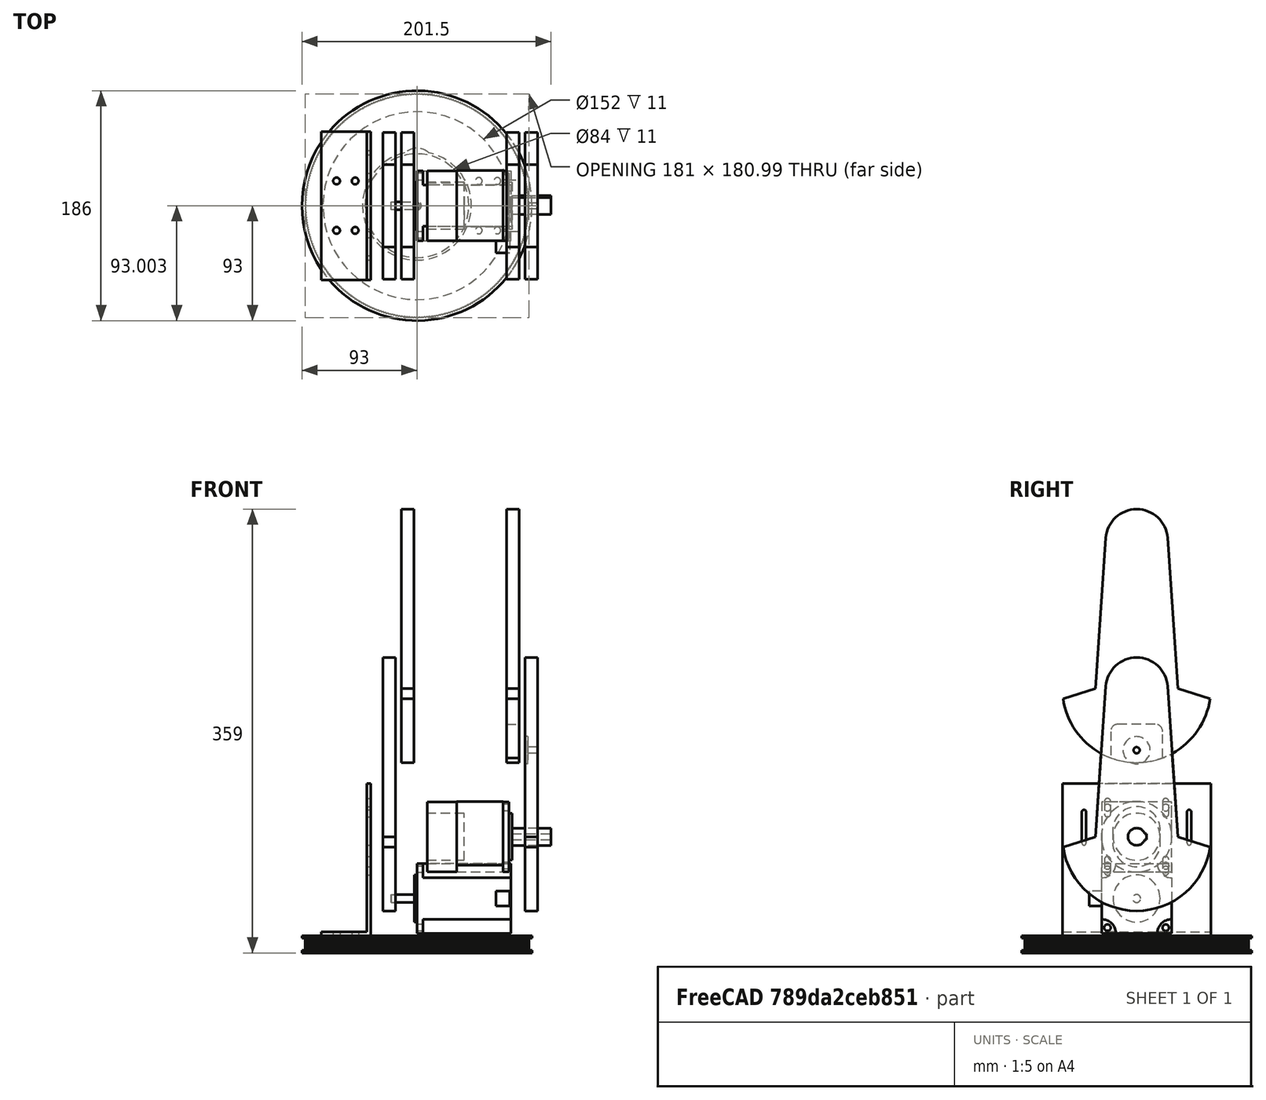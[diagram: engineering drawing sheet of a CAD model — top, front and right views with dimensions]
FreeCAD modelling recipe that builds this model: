
FCSTD DOCUMENT  (FreeCAD 0.21R33771 (Git))
Label: jrobot-y-axis-assembly
License: All rights reserved
LicenseURL: http://en.wikipedia.org/wiki/All_rights_reserved
objects: Part::Feature×26, App::Link×13, Part::MultiCommon×8, App::DocumentObjectGroup×5, App::Part×2, PartDesign::CoordinateSystem×1, App::FeaturePython×1, Part::FeaturePython×1
note: 36 computed .brp shape members not serialized (recipe doc carries the construction recipe); baked Part::Feature solids carry a one-line shape summary decoded from their .brp
EXTERNAL_REF file=jrobot-x-axis-parts.FCStd obj=LCS_X_Axis_Rotor_Origin
EXTERNAL_REF file=jrobot-x-axis-parts.FCStd obj=Part022
EXTERNAL_REF file=jrobot-x-axis-parts.FCStd obj=LCS_1
EXTERNAL_REF file=jrobot-y-axis-parts.FCStd obj=LCS_Y_Axis_Base_Left_Origin
EXTERNAL_REF file=jrobot-y-axis-parts.FCStd obj=Part
EXTERNAL_REF file=jrobot-x-axis-parts.FCStd obj=LCS_Y_Axis_Base_Right
EXTERNAL_REF file=jrobot-y-axis-parts.FCStd obj=LCS_Y_Axis_Arm_Left_Pivot
EXTERNAL_REF file=jrobot-y-axis-parts.FCStd obj=LCS_Y_Axis_Base_Pivot
EXTERNAL_REF file=jrobot-y-axis-parts.FCStd obj=Part001
EXTERNAL_REF file=jrobot-x-axis-parts.FCStd obj=LCS_X_Axis_Rotor_Top
EXTERNAL_REF file=standard-parts.FCStd obj=LCS_Nema23_76mm_MountFace
EXTERNAL_REF file=standard-parts.FCStd obj=Part015
EXTERNAL_REF file=standard-parts.FCStd obj=LCS_Nema23_Gearbox_FLF57_Origin
EXTERNAL_REF file=standard-parts.FCStd obj=Part068
EXTERNAL_REF file=jrobot-y-axis-parts.FCStd obj=LCS_Y_Axis_ZMotor
EXTERNAL_REF file=standard-parts.FCStd obj=LCS_Nema17_42mm_MountFace
EXTERNAL_REF file=standard-parts.FCStd obj=Part001
EXTERNAL_REF file=jrobot-y-axis-parts.FCStd obj=LCS_Y_Axis_ZPivot
EXTERNAL_REF file=jrobot-y-axis-parts.FCStd obj=LCS_Origin
EXTERNAL_REF file=jrobot-y-axis-parts.FCStd obj=Part002
EXTERNAL_REF file=standard-parts.FCStd obj=LCS_Bearing_Printed_Inner_Origin
EXTERNAL_REF file=standard-parts.FCStd obj=Part069
EXTERNAL_REF file=../../../snap/freecad/common/temp/FreeCAD_Doc_96e0f8cd-3bd0-4b8c-b372-3804dd1025b3_da39a3_2601561 obj=LCS_Bearing_Printed_Inner_Origin
EXTERNAL_REF file=../../../snap/freecad/common/temp/FreeCAD_Doc_96e0f8cd-3bd0-4b8c-b372-3804dd1025b3_da39a3_2601561 obj=Part069

FEATURE [App::DocumentObjectGroup] Parts
FEATURE [PartDesign::CoordinateSystem] LCS_Origin
  AttacherType = Attacher::AttachEngine3D
  MapMode = 2
  Support = -> [X_Axis]
FEATURE [App::DocumentObjectGroup] Constraints
FEATURE [App::FeaturePython] Variables  # WARN: FeaturePython — macro-defined, semantics opaque (R4)
  Type = App::PropertyContainer
FEATURE [App::DocumentObjectGroup] Configurations
FEATURE [App::Link] P_X_Axis_Rotor
  AttachedBy = #LCS_X_Axis_Rotor_Origin
  AttachedTo = Parent Assembly#LCS_Origin
  LinkedObject = -> <external jrobot-x-axis-parts.FCStd>#Part022
  SolverId = Asm4EE
  expr: Placement = LCS_Origin.Placement * AttachmentOffset * jrobot_x_axis_parts#LCS_X_Axis_Rotor_Origin.Placement ^ -1
FEATURE [App::Link] P_Y_Axis_Base_Left
  AttachedBy = #LCS_Y_Axis_Base_Left_Origin
  AttachedTo = P_X_Axis_Rotor#LCS_1
  LinkPlacement = pos=(57.5,0,14) rot=(0,0,1;0rad)
  LinkedObject = -> <external jrobot-y-axis-parts.FCStd>#Part
  Placement = pos=(57.5,0,14) rot=(0,0,1;0rad)
  SolverId = Asm4EE
  expr: Placement = P_X_Axis_Rotor.Placement * jrobot_x_axis_parts#LCS_1.Placement * AttachmentOffset * jrobot_y_axis_parts#LCS_Y_Axis_Base_Left_Origin.Placement ^ -1
FEATURE [App::Link] P_Y_Axis_Base_Left_2
  AttachedBy = #LCS_Y_Axis_Base_Left_Origin
  AttachedTo = P_X_Axis_Rotor#LCS_Y_Axis_Base_Right
  LinkPlacement = pos=(-57.5,0,14) rot=(0,0,1;0rad)
  LinkedObject = -> <external jrobot-y-axis-parts.FCStd>#Part
  Placement = pos=(-57.5,0,14) rot=(0,0,1;0rad)
  SolverId = Asm4EE
  expr: Placement = P_X_Axis_Rotor.Placement * jrobot_x_axis_parts#LCS_Y_Axis_Base_Right.Placement * AttachmentOffset * jrobot_y_axis_parts#LCS_Y_Axis_Base_Left_Origin.Placement ^ -1
FEATURE [App::Link] P_Y_Axis_Arm_Left
  AttachedBy = #LCS_Y_Axis_Arm_Left_Pivot
  AttachedTo = P_Y_Axis_Base_Left#LCS_Y_Axis_Base_Pivot
  AttachmentOffset = pos=(-20,0,0) rot=(1,0,0;0rad)
  LinkPlacement = pos=(57.5,0,154) rot=(0,0,1;0rad)
  LinkedObject = -> <external jrobot-y-axis-parts.FCStd>#Part001
  Placement = pos=(57.5,0,154) rot=(0,0,1;0rad)
  SolverId = Asm4EE
  expr: Placement = P_Y_Axis_Base_Left.Placement * jrobot_y_axis_parts#LCS_Y_Axis_Base_Pivot.Placement * AttachmentOffset * jrobot_y_axis_parts#LCS_Y_Axis_Arm_Left_Pivot.Placement ^ -1
FEATURE [App::Link] P_Nema23_76mm
  AttachedBy = #LCS_Nema23_76mm_MountFace
  AttachedTo = P_X_Axis_Rotor#LCS_X_Axis_Rotor_Top
  AttachmentOffset = pos=(30,0,30) rot=(0.57735,-0.57735,-0.57735;2.0944rad)
  LinkPlacement = pos=(106,8.4e-15,44) rot=(0.57735,-0.57735,-0.57735;2.0944rad)
  LinkedObject = -> <external standard-parts.FCStd>#Part015
  Placement = pos=(106,8.4e-15,44) rot=(0.57735,-0.57735,-0.57735;2.0944rad)
  SolverId = Asm4EE
  expr: Placement = P_X_Axis_Rotor.Placement * jrobot_x_axis_parts#LCS_X_Axis_Rotor_Top.Placement * AttachmentOffset * standard_parts#LCS_Nema23_76mm_MountFace.Placement ^ -1
FEATURE [App::Link] P_Nema23_Gearbox_FLF57
  AttachedBy = #LCS_Nema23_Gearbox_FLF57_Origin
  AttachedTo = P_Nema23_76mm#LCS_Nema23_76mm_MountFace
  AttachmentOffset = pos=(0,0,0) rot=(0,0,-1;1.5708rad)
  LinkPlacement = pos=(30,0,44) rot=(0.707107,0,-0.707107;3.14159rad)
  LinkedObject = -> <external standard-parts.FCStd>#Part068
  Placement = pos=(30,0,44) rot=(0.707107,0,-0.707107;3.14159rad)
  SolverId = Asm4EE
  expr: Placement = P_Nema23_76mm.Placement * standard_parts#LCS_Nema23_76mm_MountFace.Placement * AttachmentOffset * standard_parts#LCS_Nema23_Gearbox_FLF57_Origin.Placement ^ -1
FEATURE [App::Link] P_Nema17_33mm
  AttachedBy = #LCS_Nema17_42mm_MountFace
  AttachedTo = P_Y_Axis_Arm_Left#LCS_Y_Axis_ZMotor
  AttachmentOffset = pos=(0,0,0) rot=(0.57735,0.57735,0.57735;2.0944rad)
  LinkPlacement = pos=(24.5,1.1e-14,224) rot=(0.57735,0.57735,0.57735;2.0944rad)
  LinkedObject = -> <external standard-parts.FCStd>#Part001
  Placement = pos=(24.5,1.1e-14,224) rot=(0.57735,0.57735,0.57735;2.0944rad)
  SolverId = Asm4EE
  expr: Placement = P_Y_Axis_Arm_Left.Placement * jrobot_y_axis_parts#LCS_Y_Axis_ZMotor.Placement * AttachmentOffset * standard_parts#LCS_Nema17_42mm_MountFace.Placement ^ -1
FEATURE [App::Link] P_Y_Axis_Base_Left001
  AttachedBy = #LCS_Y_Axis_Base_Left_Origin
  AttachedTo = P_X_Axis_Rotor#LCS_Y_Axis_Base_Right
  LinkPlacement = pos=(-57.5,0,14) rot=(0,0,1;0rad)
  LinkedObject = -> <external jrobot-y-axis-parts.FCStd>#Part
  Placement = pos=(-57.5,0,14) rot=(0,0,1;0rad)
  SolverId = Asm4EE
  expr: Placement = P_X_Axis_Rotor.Placement * jrobot_x_axis_parts#LCS_Y_Axis_Base_Right.Placement * AttachmentOffset * jrobot_y_axis_parts#LCS_Y_Axis_Base_Left_Origin.Placement ^ -1
FEATURE [App::Link] P_Y_Axis_Arm_Left001
  AttachedBy = #LCS_Y_Axis_Arm_Left_Pivot
  AttachedTo = P_Y_Axis_Base_Left001#LCS_Y_Axis_Base_Pivot
  AttachmentOffset = pos=(10,0,0) rot=(0,0,1;0rad)
  LinkPlacement = pos=(-27.5,0,154) rot=(0,0,1;0rad)
  LinkedObject = -> <external jrobot-y-axis-parts.FCStd>#Part001
  Placement = pos=(-27.5,0,154) rot=(0,0,1;0rad)
  SolverId = Asm4EE
  expr: Placement = P_Y_Axis_Base_Left001.Placement * jrobot_y_axis_parts#LCS_Y_Axis_Base_Pivot.Placement * AttachmentOffset * jrobot_y_axis_parts#LCS_Y_Axis_Arm_Left_Pivot.Placement ^ -1
FEATURE [App::Link] P_Y_Axis_Arm_Left002
  AttachedBy = #LCS_Y_Axis_Arm_Left_Pivot
  AttachedTo = P_Y_Axis_Arm_Left001#LCS_Y_Axis_ZPivot
  AttachmentOffset = pos=(15,0,0) rot=(0,0,1;0rad)
  LinkPlacement = pos=(-12.5,0,274) rot=(0,0,1;0rad)
  LinkedObject = -> <external jrobot-y-axis-parts.FCStd>#Part001
  Placement = pos=(-12.5,0,274) rot=(0,0,1;0rad)
  SolverId = Asm4EE
  expr: Placement = P_Y_Axis_Arm_Left001.Placement * jrobot_y_axis_parts#LCS_Y_Axis_ZPivot.Placement * AttachmentOffset * jrobot_y_axis_parts#LCS_Y_Axis_Arm_Left_Pivot.Placement ^ -1
FEATURE [App::Link] P_Y_Axis_Arm_1
  AttachedBy = #LCS_Y_Axis_Arm_Left_Pivot
  AttachedTo = P_Y_Axis_Arm_Left#LCS_Y_Axis_ZPivot
  AttachmentOffset = pos=(-15,0,0) rot=(0,0,1;0rad)
  LinkPlacement = pos=(42.5,0,274) rot=(0,0,1;0rad)
  LinkedObject = -> <external jrobot-y-axis-parts.FCStd>#Part001
  Placement = pos=(42.5,0,274) rot=(0,0,1;0rad)
  SolverId = Asm4EE
  expr: Placement = P_Y_Axis_Arm_Left.Placement * jrobot_y_axis_parts#LCS_Y_Axis_ZPivot.Placement * AttachmentOffset * jrobot_y_axis_parts#LCS_Y_Axis_Arm_Left_Pivot.Placement ^ -1
FEATURE [Part::Feature] P_X_Axis_Rotor001
  shape: bbox 2e+100 x 2e+100 x 14 mm, 883 faces (baked)
FEATURE [Part::Feature] P_Y_Axis_Base_Left002
  Placement = pos=(57.5,0,14) rot=(0,0,1;0rad)
  shape: bbox 2e+100 x 2e+100 x 123 mm, 50 faces (baked)
FEATURE [Part::Feature] P_Y_Axis_Arm_Left003
  Placement = pos=(87.5,0,94) rot=(0,0,1;0rad)
  shape: bbox 10 x 118.8 x 205 mm, 8 faces (baked)
FEATURE [Part::Feature] P_Nema23_76mm001
  Placement = pos=(76,8e-15,44) rot=(0.57735,-0.57735,-0.57735;2.0944rad)
  shape: bbox 2e+100 x 2e+100 x 2e+100 mm, 28 faces (baked)
FEATURE [Part::Feature] P_Nema23_Gearbox_FLF058
  Placement = pos=(8.2,0,94) rot=(0,1,0;1.5708rad)
  shape: bbox 100.3 x 2e+100 x 2e+100 mm, 42 faces (baked)
FEATURE [Part::Feature] P_X_Axis_Rotor002
  shape: bbox 2e+100 x 2e+100 x 14 mm, 883 faces (baked)
FEATURE [Part::Feature] P_Nema23_Gearbox_FLF059
  Placement = pos=(8.2,0,94) rot=(0,1,0;1.5708rad)
  shape: bbox 100.3 x 2e+100 x 2e+100 mm, 42 faces (baked)
FEATURE [Part::MultiCommon] Common  label="Common 1 - 4 - P_X_Axis_Rotor002 - P_Nema23_Gearbox_FLF059"
  Shapes = -> [P_X_Axis_Rotor002,P_Nema23_Gearbox_FLF059]
FEATURE [Part::Feature] P_Nema17_33mm001
  Placement = pos=(54.5,1.1e-14,164) rot=(0.57735,0.57735,0.57735;2.0944rad)
  shape: bbox 2e+100 x 2e+100 x 2e+100 mm, 28 faces (baked)
FEATURE [Part::Feature] P_Y_Axis_Base_Left003
  Placement = pos=(-57.5,0,14) rot=(0,0,1;0rad)
  shape: bbox 2e+100 x 2e+100 x 123 mm, 50 faces (baked)
FEATURE [Part::Feature] P_Y_Axis_Arm_Left004
  Placement = pos=(-27.5,-7e-15,94) rot=(0,0,1;0rad)
  shape: bbox 10 x 118.8 x 205 mm, 8 faces (baked)
FEATURE [Part::Feature] P_Y_Axis_Arm_Left005
  Placement = pos=(-12.5,-1.1e-14,214) rot=(0,0,1;0rad)
  shape: bbox 10 x 118.8 x 205 mm, 8 faces (baked)
FEATURE [Part::Feature] P_Y_Axis_Arm_002
  Placement = pos=(72.5,0,214) rot=(0,0,1;0rad)
  shape: bbox 10 x 118.8 x 205 mm, 8 faces (baked)
FEATURE [App::Part] Assembly_copy
  Group = -> [P_X_Axis_Rotor001,P_Y_Axis_Base_Left002,P_Y_Axis_Arm_Left003,P_Nema23_76mm001,P_Nema23_Gearbox_FLF058,P_Nema17_33mm001,P_Y_Axis_Base_Left003,P_Y_Axis_Arm_Left004,P_Y_Axis_Arm_Left005,P_Y_Axis_Arm_002]
  Origin = -> Origin001
FEATURE [Part::Feature] P_Y_Axis_Base_Left004
  Placement = pos=(57.5,0,14) rot=(0,0,1;0rad)
  shape: bbox 2e+100 x 2e+100 x 123 mm, 50 faces (baked)
FEATURE [Part::Feature] P_Nema23_Gearbox_FLF060
  Placement = pos=(8.2,0,94) rot=(0,1,0;1.5708rad)
  shape: bbox 100.3 x 2e+100 x 2e+100 mm, 42 faces (baked)
FEATURE [Part::MultiCommon] Common001  label="Common 2 - 12 - P_Y_Axis_Base_Left004 - P_Nema23_Gearbox_FLF060"
  Shapes = -> [P_Y_Axis_Base_Left004,P_Nema23_Gearbox_FLF060]
FEATURE [Part::Feature] P_Y_Axis_Base_Left005
  Placement = pos=(57.5,0,14) rot=(0,0,1;0rad)
  shape: bbox 2e+100 x 2e+100 x 123 mm, 50 faces (baked)
FEATURE [Part::Feature] P_Y_Axis_Base_Left006
  Placement = pos=(-57.5,0,14) rot=(0,0,1;0rad)
  shape: bbox 2e+100 x 2e+100 x 123 mm, 50 faces (baked)
FEATURE [Part::MultiCommon] Common002  label="Common 3 - 14 - P_Y_Axis_Base_Left005 - P_Y_Axis_Base_Left006"
  Shapes = -> [P_Y_Axis_Base_Left005,P_Y_Axis_Base_Left006]
FEATURE [Part::Feature] P_Y_Axis_Arm_Left006
  Placement = pos=(87.5,0,94) rot=(0,0,1;0rad)
  shape: bbox 10 x 118.8 x 205 mm, 8 faces (baked)
FEATURE [Part::Feature] P_Nema23_Gearbox_FLF061
  Placement = pos=(8.2,0,94) rot=(0,1,0;1.5708rad)
  shape: bbox 100.3 x 2e+100 x 2e+100 mm, 42 faces (baked)
FEATURE [Part::MultiCommon] Common003  label="Common 4 - 19 - P_Y_Axis_Arm_Left006 - P_Nema23_Gearbox_FLF061"
  Shapes = -> [P_Y_Axis_Arm_Left006,P_Nema23_Gearbox_FLF061]
FEATURE [Part::Feature] P_Y_Axis_Arm_Left007
  Placement = pos=(87.5,0,94) rot=(0,0,1;0rad)
  shape: bbox 10 x 118.8 x 205 mm, 8 faces (baked)
FEATURE [Part::Feature] P_Nema17_33mm002
  Placement = pos=(54.5,1.1e-14,164) rot=(0.57735,0.57735,0.57735;2.0944rad)
  shape: bbox 2e+100 x 2e+100 x 2e+100 mm, 28 faces (baked)
FEATURE [Part::MultiCommon] Common004  label="Common 5 - 20 - P_Y_Axis_Arm_Left007 - P_Nema17_33mm002"
  Shapes = -> [P_Y_Axis_Arm_Left007,P_Nema17_33mm002]
FEATURE [Part::Feature] P_Nema23_76mm002
  Placement = pos=(76,8e-15,44) rot=(0.57735,-0.57735,-0.57735;2.0944rad)
  shape: bbox 2e+100 x 2e+100 x 2e+100 mm, 28 faces (baked)
FEATURE [Part::Feature] P_Nema23_Gearbox_FLF062
  Placement = pos=(8.2,0,94) rot=(0,1,0;1.5708rad)
  shape: bbox 100.3 x 2e+100 x 2e+100 mm, 42 faces (baked)
FEATURE [Part::MultiCommon] Common005  label="Common 6 - 25 - P_Nema23_76mm002 - P_Nema23_Gearbox_FLF062"
  Shapes = -> [P_Nema23_76mm002,P_Nema23_Gearbox_FLF062]
FEATURE [Part::Feature] P_Nema23_76mm003
  Placement = pos=(76,8e-15,44) rot=(0.57735,-0.57735,-0.57735;2.0944rad)
  shape: bbox 2e+100 x 2e+100 x 2e+100 mm, 28 faces (baked)
FEATURE [Part::Feature] P_Y_Axis_Arm_Left008
  Placement = pos=(-27.5,-7e-15,94) rot=(0,0,1;0rad)
  shape: bbox 10 x 118.8 x 205 mm, 8 faces (baked)
FEATURE [Part::MultiCommon] Common006  label="Common 7 - 28 - P_Nema23_76mm003 - P_Y_Axis_Arm_Left008"
  Shapes = -> [P_Nema23_76mm003,P_Y_Axis_Arm_Left008]
FEATURE [Part::Feature] P_Nema17_33mm003
  Placement = pos=(54.5,1.1e-14,164) rot=(0.57735,0.57735,0.57735;2.0944rad)
  shape: bbox 2e+100 x 2e+100 x 2e+100 mm, 28 faces (baked)
FEATURE [Part::Feature] P_Y_Axis_Arm_003
  Placement = pos=(72.5,0,214) rot=(0,0,1;0rad)
  shape: bbox 10 x 118.8 x 205 mm, 8 faces (baked)
FEATURE [Part::MultiCommon] Common007  label="Common 8 - 39 - P_Nema17_33mm003 - P_Y_Axis_Arm_003"
  Shapes = -> [P_Nema17_33mm003,P_Y_Axis_Arm_003]
FEATURE [App::DocumentObjectGroup] Intersections
  Group = -> [Common,Common001,Common002,Common003,Common004,Common005,Common006,Common007]
FEATURE [App::DocumentObjectGroup] Interferences
  Group = -> [Assembly_copy,Intersections]
FEATURE [App::Link] P_Y_Axis_RotorWheel001
  AttachedBy = #LCS_Origin
  AttachedTo = P_Y_Axis_Arm_Left001#LCS_Y_Axis_Arm_Left_Pivot
  AttachmentOffset = pos=(-40,0,0) rot=(0,0,1;0rad)
  LinkPlacement = pos=(-67.5,0,154) rot=(0,0,1;0rad)
  LinkedObject = -> <external jrobot-y-axis-parts.FCStd>#Part002
  Placement = pos=(-67.5,0,154) rot=(0,0,1;0rad)
  SolverId = Asm4EE
  expr: Placement = P_Y_Axis_Arm_Left001.Placement * jrobot_y_axis_parts#LCS_Y_Axis_Arm_Left_Pivot.Placement * AttachmentOffset * jrobot_y_axis_parts#LCS_Origin.Placement ^ -1
FEATURE [App::Link] P_Bearing_Printed_Inner_6mm_13mm_3_5mm  label="P_Bearing_Printed_Inner_6mm_13mm_3.5mm"
  AttachedBy = #LCS_Bearing_Printed_Inner_Origin
  AttachedTo = P_Y_Axis_Arm_Left001#LCS_Y_Axis_ZPivot
  LinkPlacement = pos=(-27.5,0,274) rot=(0,0,1;0rad)
  LinkedObject = -> <external standard-parts.FCStd>#Part069
  Placement = pos=(-27.5,0,274) rot=(0,0,1;0rad)
  SolverId = Asm4EE
  expr: Placement = P_Y_Axis_Arm_Left001.Placement * jrobot_y_axis_parts#LCS_Y_Axis_ZPivot.Placement * AttachmentOffset * standard_parts#LCS_Bearing_Printed_Inner_Origin.Placement ^ -1
FEATURE [Part::FeaturePython] P_Bearing_Printed_Inner_6mm_13mm_3_5mm_var  label="P_Bearing_Printed_Inner_6mm_13mm_3.5mm_var"  # link proxy (typed FeaturePython)
  AttachedBy = #LCS_Bearing_Printed_Inner_Origin
  AttachedTo = P_Y_Axis_Arm_1#LCS_Y_Axis_Arm_Left_Pivot
  LinkedObject = -> <external ../../../snap/freecad/common/temp/FreeCAD_Doc_96e0f8cd-3bd0-4b8c-b372-3804dd1025b3_da39a3_2601561>#Part069
  Placement = pos=(42.5,0,274) rot=(0,0,1;0rad)
  SolverId = Asm4EE
  SourceObject = -> <external standard-parts.FCStd>#Part069
  Type = Asm4::VariantLink
  expr: Placement = P_Y_Axis_Arm_1.Placement * jrobot_y_axis_parts#LCS_Y_Axis_Arm_Left_Pivot.Placement * AttachmentOffset * varTmpDoc_1#LCS_Bearing_Printed_Inner_Origin.Placement ^ -1
FEATURE [App::Part] Assembly
  AssemblyType = Part::Link
  Group = -> [LCS_Origin,Constraints,Variables,Configurations,P_X_Axis_Rotor,P_Y_Axis_Base_Left,P_Y_Axis_Base_Left_2,P_Y_Axis_Arm_Left,P_Nema23_76mm,P_Nema23_Gearbox_FLF57,P_Nema17_33mm,P_Y_Axis_Base_Left001,P_Y_Axis_Arm_Left001,P_Y_Axis_Arm_Left002,P_Y_Axis_Arm_1,P_Y_Axis_RotorWheel001,P_Bearing_Printed_Inner_6mm_13mm_3_5mm,P_Bearing_Printed_Inner_6mm_13mm_3_5mm_var]
  Origin = -> Origin
  Type = Assembly

RESOLVED EXTERNAL PARTS (link-assembly join: the EXTERNAL_REF files above that resolve inside this repo's crawl, each included once):
---- part jrobot-x-axis-parts.FCStd = doc fcstd_4231072843c4 (96222 chars; too large to inline — full recipe in that document) ----
---- part jrobot-y-axis-parts.FCStd = doc fcstd_3b5a0104af3e ----
FCSTD DOCUMENT  (FreeCAD 0.21R33771 (Git))
Label: jrobot-y-axis-parts
License: All rights reserved
LicenseURL: http://en.wikipedia.org/wiki/All_rights_reserved
objects: PartDesign::CoordinateSystem×11, Sketcher::SketchObject×9, PartDesign::Pad×6, PartDesign::Body×3, App::Part×3, PartDesign::Pocket×2, PartDesign::Hole×1, App::DocumentObjectGroup×1
note: 41 computed .brp shape members not serialized (recipe doc carries the construction recipe); baked Part::Feature solids carry a one-line shape summary decoded from their .brp

FEATURE [Sketcher::SketchObject] Sketch
  FullyConstrained = true
  MapMode = 5
  Support = -> [XY_Plane001]
  sketch-geometry (4):
    g0: LineSegment StartX=-20 StartY=60 StartZ=0 EndX=20 EndY=60 EndZ=0
    g1: LineSegment StartX=20 StartY=60 StartZ=0 EndX=20 EndY=-60 EndZ=0
    g2: LineSegment StartX=20 StartY=-60 StartZ=0 EndX=-20 EndY=-60 EndZ=0
    g3: LineSegment StartX=-20 StartY=-60 StartZ=0 EndX=-20 EndY=60 EndZ=0
  constraints (10):
    c: Coincident(g0,g1)
    c: Coincident(g1,g2)
    c: Coincident(g2,g3)
    c: Coincident(g3,g0)
    c: Horizontal(g2)
    c: Vertical(g1)
    c: Symmetric(g0,g0,g-2)
    c: Symmetric(g0,g2,g-1)
    c: DistanceX(g0,g0) = 40
    c: DistanceY(g3,g3) = 120
FEATURE [PartDesign::Pad] Pad
  Direction = (0,0,1)
  Length = 3
  Length2 = 10
  Profile = -> Sketch
  ReferenceAxis = -> Sketch [N_Axis]
  Type = 0
FEATURE [Sketcher::SketchObject] Sketch001
  AttachmentOffset = pos=(0,0,3) rot=(0,0,1;0rad)
  FullyConstrained = true
  MapMode = 5
  Placement = pos=(0,0,3) rot=(0,0,1;0rad)
  Support = -> [XY_Plane001]
  sketch-geometry (4):
    g0: Circle CenterX=-7.5 CenterY=20 CenterZ=0 NormalX=0 NormalY=0 NormalZ=1 AngleXU=0 Radius=2.5
    g1: Circle CenterX=7.5 CenterY=20 CenterZ=0 NormalX=0 NormalY=0 NormalZ=1 AngleXU=0 Radius=2.5
    g2: Circle CenterX=-7.5 CenterY=-20 CenterZ=0 NormalX=0 NormalY=0 NormalZ=1 AngleXU=0 Radius=2.5
    g3: Circle CenterX=7.5 CenterY=-20 CenterZ=0 NormalX=0 NormalY=0 NormalZ=1 AngleXU=0 Radius=2.5
  constraints (10):
    c: Horizontal(g3,g2)
    c: Vertical(g1,g3)
    c: Equal(g0,g1)
    c: Equal(g1,g3)
    c: Equal(g3,g2)
    c: Diameter(g0) = 5
    c: Symmetric(g0,g2,g-1)
    c: Symmetric(g0,g1,g-2)
    c: DistanceX(g2,g3) = 15
    c: DistanceY(g2,g0) = 40
FEATURE [PartDesign::Hole] Hole
  BaseFeature = -> Pad
  CustomThreadClearance = 0
  Depth = 25
  DepthType = 0
  Diameter = 5.5
  DrillForDepth = false
  DrillPoint = 1
  DrillPointAngle = 118
  HoleCutCountersinkAngle = 90
  HoleCutCustomValues = false
  HoleCutDepth = 0
  HoleCutDiameter = 6.1
  HoleCutType = 0
  ModelThread = false
  Profile = -> Sketch001
  Tapered = false
  TaperedAngle = 90
  ThreadClass = 0
  ThreadDepth = 25
  ThreadDepthType = 0
  ThreadDirection = 0
  ThreadFit = 0
  ThreadSize = 13
  ThreadType = 1
  Threaded = false
  UseCustomThreadClearance = false
FEATURE [PartDesign::CoordinateSystem] LCS_Y_Axis_Base_Left_Bolt0  label="LCS_Y_Axis_Base_Left_Bolt1"
  AttacherType = Attacher::AttachEngine3D
  MapMode = 11
  Placement = pos=(-7.5,-20,3) rot=(0,0,1;1.5708rad)
  Support = -> [Hole]
FEATURE [PartDesign::CoordinateSystem] LCS_Y_Axis_Base_Left_Bolt1  label="LCS_Y_Axis_Base_Left_Bolt0"
  AttacherType = Attacher::AttachEngine3D
  MapMode = 11
  Placement = pos=(-7.5,20,3) rot=(0,0,1;1.5708rad)
  Support = -> [Sketch001]
FEATURE [PartDesign::CoordinateSystem] LCS_Y_Axis_Base_Left_Bolt2
  AttacherType = Attacher::AttachEngine3D
  MapMode = 11
  Placement = pos=(7.5,20,3) rot=(0,0,1;1.5708rad)
  Support = -> [Hole]
FEATURE [PartDesign::CoordinateSystem] LCS_Y_Axis_Base_Left_Bolt3
  AttacherType = Attacher::AttachEngine3D
  MapMode = 11
  Placement = pos=(7.5,-20,3) rot=(0,0,1;1.5708rad)
  Support = -> [Hole]
FEATURE [PartDesign::CoordinateSystem] LCS_Y_Axis_Base_Left_Origin
  AttacherType = Attacher::AttachEngine3D
FEATURE [Sketcher::SketchObject] Sketch002
  AttachmentOffset = pos=(0,0,3) rot=(0,0,1;0rad)
  FullyConstrained = true
  MapMode = 5
  Placement = pos=(0,0,3) rot=(0,0,1;0rad)
  Support = -> [XY_Plane001]
  sketch-geometry (4):
    g0: LineSegment StartX=17 StartY=60 StartZ=0 EndX=20 EndY=60 EndZ=0
    g1: LineSegment StartX=20 StartY=60 StartZ=0 EndX=20 EndY=-60 EndZ=0
    g2: LineSegment StartX=20 StartY=-60 StartZ=0 EndX=17 EndY=-60 EndZ=0
    g3: LineSegment StartX=17 StartY=-60 StartZ=0 EndX=17 EndY=60 EndZ=0
  constraints (11):
    c: Coincident(g0,g1)
    c: Coincident(g1,g2)
    c: Coincident(g2,g3)
    c: Coincident(g3,g0)
    c: Horizontal(g0)
    c: Horizontal(g2)
    c: Vertical(g1)
    c: DistanceY(g1,g1) = 120
    c: DistanceX(g-1,g1) = 20
    c: DistanceX(g2,g2) = 3
    c: Symmetric(g2,g0,g-1)
FEATURE [PartDesign::Pad] Pad001
  BaseFeature = -> Hole
  Direction = (0,0,1)
  Length = 200
  Length2 = 10
  Profile = -> Sketch002
  ReferenceAxis = -> Sketch002 [N_Axis]
  Type = 0
FEATURE [Sketcher::SketchObject] Sketch003
  FullyConstrained = false
  MapMode = 5
  Placement = pos=(0,0,0) rot=(0.57735,0.57735,0.57735;2.0944rad)
  Support = -> [YZ_Plane003]
  sketch-geometry (6):
    g0: ArcOfCircle CenterX=-0.0718095 CenterY=300 CenterZ=0 NormalX=0 NormalY=0 NormalZ=1 AngleXU=0 Radius=25 StartAngle=0.0279955 EndAngle=3.11407
    g1: LineSegment StartX=24.9184 StartY=300.7 StartZ=0 EndX=33.3388 EndY=0 EndZ=0
    g2: LineSegment StartX=-25.0623 StartY=300.688 StartZ=0 EndX=-33.3388 EndY=0 EndZ=0
    g3: LineSegment StartX=-33.3388 StartY=0 StartZ=0 EndX=-63.4439 EndY=-48.7326 EndZ=0
    g4: LineSegment StartX=33.3388 StartY=0 StartZ=0 EndX=63.4439 EndY=-48.7326 EndZ=0
    g5: ArcOfCircle CenterX=0 CenterY=0 CenterZ=0 NormalX=0 NormalY=0 NormalZ=1 AngleXU=0 Radius=80 StartAngle=3.79659 EndAngle=5.62819
  constraints (13):
    c: Tangent(g2,g0) = -1.5708
    c: Tangent(g1,g0) = 1.5708
    c: Diameter(g0) = 50
    c: Coincident(g3,g2)
    c: Coincident(g4,g1)
    c: Horizontal(g4,g3)
    c: Horizontal(g1,g-1)
    c: Symmetric(g2,g1,g-2)
    c: DistanceY(g-1,g0) = 300
    c: Coincident(g5,g3)
    c: Coincident(g4,g5)
    c: Diameter(g5) = 160
    c: Coincident(g5,g-1)
FEATURE [PartDesign::Pad] Pad002
  Direction = (1,-2e-16,3e-16)
  Length = 10
  Length2 = 10
  Placement = pos=(0,0,0) rot=(0.57735,0.57735,0.57735;2.0944rad)
  Profile = -> Sketch003
  ReferenceAxis = -> Sketch003 [N_Axis]
  Type = 0
FEATURE [PartDesign::Body] Body001  label="B_Y_Axis_Arm_Left"
  Group = -> [Sketch003,Pad002]
  Origin = -> Origin003
  Tip = -> Pad002
FEATURE [PartDesign::CoordinateSystem] LCS_Y_Axis_Base_Pivot
  AttacherType = Attacher::AttachEngine3D
  Placement = pos=(20,0,140) rot=(0,0,1;0rad)
FEATURE [PartDesign::CoordinateSystem] LCS_Y_Axis_Arm_Left_Pivot
  AttacherType = Attacher::AttachEngine3D
FEATURE [PartDesign::CoordinateSystem] LCS_Y_Axis_Base_Left_MotorMount
  AttacherType = Attacher::AttachEngine3D
  Placement = pos=(17,0,80) rot=(0,0,1;0rad)
FEATURE [PartDesign::CoordinateSystem] LCS_Y_Axis_ZMotor
  AttacherType = Attacher::AttachEngine3D
  Placement = pos=(0,0,70) rot=(0,0,1;0rad)
FEATURE [PartDesign::CoordinateSystem] LCS_Y_Axis_ZPivot
  AttacherType = Attacher::AttachEngine3D
  Placement = pos=(0,0,120) rot=(0,0,1;0rad)
FEATURE [App::Part] Part001  label="P_Y_Axis_Arm_Left"
  Group = -> [Body001,LCS_Y_Axis_Arm_Left_Pivot,LCS_Y_Axis_ZMotor,LCS_Y_Axis_ZPivot]
  Origin = -> Origin002
FEATURE [Sketcher::SketchObject] Sketch104  label="S_Y_Axis_MotorMount_Slots"
  AttachmentOffset = pos=(0,140,20) rot=(0,0,1;0rad)
  FullyConstrained = true
  MapMode = 4
  Placement = pos=(20,0,140) rot=(0.57735,0.57735,0.57735;2.0944rad)
  Support = -> [Part001]
  sketch-geometry (28):
    g0: ArcOfCircle CenterX=-23.5 CenterY=28.5 CenterZ=0 NormalX=0 NormalY=0 NormalZ=1 AngleXU=0 Radius=2.5 StartAngle=0 EndAngle=3.14159
    g1: ArcOfCircle CenterX=-23.5 CenterY=18.5 CenterZ=0 NormalX=0 NormalY=0 NormalZ=1 AngleXU=0 Radius=2.5 StartAngle=3.14159 EndAngle=6.28319
    g2: LineSegment StartX=-26 StartY=28.5 StartZ=0 EndX=-26 EndY=18.5 EndZ=0
    g3: LineSegment StartX=-21 StartY=18.5 StartZ=0 EndX=-21 EndY=28.5 EndZ=0
    g4: ArcOfCircle CenterX=23.5 CenterY=28.5 CenterZ=0 NormalX=0 NormalY=0 NormalZ=1 AngleXU=0 Radius=2.5 StartAngle=3e-16 EndAngle=3.14159
    g5: ArcOfCircle CenterX=23.5 CenterY=18.5 CenterZ=0 NormalX=0 NormalY=0 NormalZ=1 AngleXU=0 Radius=2.5 StartAngle=3.14159 EndAngle=6.28319
    g6: LineSegment StartX=21 StartY=28.5 StartZ=0 EndX=21 EndY=18.5 EndZ=0
    g7: LineSegment StartX=26 StartY=18.5 StartZ=0 EndX=26 EndY=28.5 EndZ=0
    g8: ArcOfCircle CenterX=23.5 CenterY=-18.5 CenterZ=0 NormalX=0 NormalY=0 NormalZ=1 AngleXU=0 Radius=2.5 StartAngle=6e-16 EndAngle=3.14159
    g9: ArcOfCircle CenterX=23.5 CenterY=-28.5 CenterZ=0 NormalX=0 NormalY=0 NormalZ=1 AngleXU=0 Radius=2.5 StartAngle=3.14159 EndAngle=6.28319
    g10: LineSegment StartX=21 StartY=-18.5 StartZ=0 EndX=21 EndY=-28.5 EndZ=0
    g11: LineSegment StartX=26 StartY=-28.5 StartZ=0 EndX=26 EndY=-18.5 EndZ=0
    g12: ArcOfCircle CenterX=-23.5 CenterY=-18.5 CenterZ=0 NormalX=0 NormalY=0 NormalZ=1 AngleXU=0 Radius=2.5 StartAngle=0 EndAngle=3.14159
    g13: ArcOfCircle CenterX=-23.5 CenterY=-28.5 CenterZ=0 NormalX=0 NormalY=0 NormalZ=1 AngleXU=0 Radius=2.5 StartAngle=3.14159 EndAngle=6.28319
    g14: LineSegment StartX=-26 StartY=-18.5 StartZ=0 EndX=-26 EndY=-28.5 EndZ=0
    g15: LineSegment StartX=-21 StartY=-28.5 StartZ=0 EndX=-21 EndY=-18.5 EndZ=0
    g16: ArcOfCircle CenterX=-1e-16 CenterY=5 CenterZ=0 NormalX=0 NormalY=0 NormalZ=1 AngleXU=0 Radius=19.25 StartAngle=0 EndAngle=3.14159
    g17: ArcOfCircle CenterX=1e-16 CenterY=-5 CenterZ=0 NormalX=0 NormalY=0 NormalZ=1 AngleXU=0 Radius=19.25 StartAngle=3.14159 EndAngle=6.28319
    g18: LineSegment StartX=-19.25 StartY=5 StartZ=0 EndX=-19.25 EndY=-5 EndZ=0
    g19: LineSegment StartX=19.25 StartY=-5 StartZ=0 EndX=19.25 EndY=5 EndZ=0
    g20: ArcOfCircle CenterX=-42.5 CenterY=20 CenterZ=0 NormalX=0 NormalY=0 NormalZ=1 AngleXU=0 Radius=1.75 StartAngle=-9.41e-14 EndAngle=3.14159
    g21: ArcOfCircle CenterX=-42.5 CenterY=-5 CenterZ=0 NormalX=0 NormalY=0 NormalZ=1 AngleXU=0 Radius=1.75 StartAngle=3.14159 EndAngle=6.28319
    g22: LineSegment StartX=-44.25 StartY=20 StartZ=0 EndX=-44.25 EndY=-5 EndZ=0
    g23: LineSegment StartX=-40.75 StartY=-5 StartZ=0 EndX=-40.75 EndY=20 EndZ=0
    g24: ArcOfCircle CenterX=42.5 CenterY=20 CenterZ=0 NormalX=0 NormalY=0 NormalZ=1 AngleXU=0 Radius=1.75 StartAngle=7.2e-15 EndAngle=3.14159
    g25: ArcOfCircle CenterX=42.5 CenterY=-5 CenterZ=0 NormalX=0 NormalY=0 NormalZ=1 AngleXU=0 Radius=1.75 StartAngle=3.14159 EndAngle=6.28319
    g26: LineSegment StartX=40.75 StartY=20 StartZ=0 EndX=40.75 EndY=-5 EndZ=0
    g27: LineSegment StartX=44.25 StartY=-5 StartZ=0 EndX=44.25 EndY=20 EndZ=0
  constraints (67):
    c: Tangent(g0,g2) = -1.5708
    c: Tangent(g2,g1) = -1.5708
    c: Tangent(g1,g3) = -1.5708
    c: Tangent(g3,g0) = -1.5708
    c: Equal(g0,g1)
    c: Vertical(g2)
    c: Tangent(g4,g6) = -1.5708
    c: Tangent(g6,g5) = -1.5708
    c: Tangent(g5,g7) = -1.5708
    c: Tangent(g7,g4) = -1.5708
    c: Equal(g4,g5)
    c: Vertical(g6)
    c: Tangent(g8,g10) = -1.5708
    c: Tangent(g10,g9) = -1.5708
    c: Tangent(g9,g11) = -1.5708
    c: Tangent(g11,g8) = -1.5708
    c: Equal(g8,g9)
    c: Tangent(g12,g14) = -1.5708
    c: Tangent(g14,g13) = -1.5708
    c: Tangent(g13,g15) = -1.5708
    c: Tangent(g15,g12) = -1.5708
    c: Equal(g12,g13)
    c: DistanceX(g0,g4) = 47
    c: DistanceY(g12,g0) = 47
    c: Vertical(g0,g12)
    c: Vertical(g8,g4)
    c: Vertical(g11)
    c: Vertical(g15)
    c: DistanceY(g1,g0) = 10
    c: DistanceY(g5,g4) = 10
    c: DistanceY(g9,g8) = 10
    c: DistanceY(g13,g12) = 10
    c: Equal(g12,g0)
    c: Equal(g0,g4)
    c: Equal(g4,g8)
    c: Horizontal(g12,g8)
    c: Horizontal(g0,g4)
    c: DistanceX(g1,g1) = 5
    c: Symmetric(g0,g9,g-1)
    c: Tangent(g16,g18) = -1.5708
    c: Tangent(g18,g17) = -1.5708
    c: Tangent(g17,g19) = -1.5708
    c: Tangent(g19,g16) = -1.5708
    c: Equal(g16,g17)
    c: Vertical(g18)
    c: Symmetric(g16,g17,g-1)
    c: DistanceY(g17,g16) = 10
    c: Diameter(g16) = 38.5
    c: Tangent(g20,g22) = -1.5708
    c: Tangent(g22,g21) = -1.5708
    c: Tangent(g21,g23) = -1.5708
    c: Tangent(g23,g20) = -1.5708
    c: Equal(g20,g21)
    c: Vertical(g22)
    c: Tangent(g24,g26) = -1.5708
    c: Tangent(g26,g25) = -1.5708
    c: Tangent(g25,g27) = -1.5708
    c: Tangent(g27,g24) = -1.5708
    c: Equal(g24,g25)
    c: Vertical(g26)
    c: DistanceX(g25,g25) = 3.5
    c: DistanceX(g21,g21) = 3.5
    c: DistanceX(g20,g-1) = 42.5
    c: Horizontal(g21,g25)
    c: DistanceY(g22,g22) = 25
    c: DistanceY(g-1,g20) = 20
    c: Symmetric(g24,g20,g-2)
FEATURE [PartDesign::Pocket] Pocket
  BaseFeature = -> Pad001
  Direction = (-1,0,0)
  Length = 5
  Length2 = 5
  Profile = -> Sketch104
  ReferenceAxis = -> Sketch104 [N_Axis]
  Type = 0
FEATURE [Sketcher::SketchObject] Sketch105
  AttachmentOffset = pos=(0,0,20) rot=(0,0,1;0rad)
  FullyConstrained = false
  MapMode = 5
  Placement = pos=(20,-4.4e-15,4.4e-15) rot=(0.57735,0.57735,0.57735;2.0944rad)
  Support = -> [YZ_Plane001]
  sketch-geometry (6):
    g0: ArcOfCircle CenterX=0 CenterY=142.229 CenterZ=0 NormalX=0 NormalY=0 NormalZ=1 AngleXU=0 Radius=113.119 StartAngle=0.0137959 EndAngle=3.15539
    g1: ArcOfCircle CenterX=0 CenterY=142.229 CenterZ=0 NormalX=0 NormalY=0 NormalZ=1 AngleXU=0 Radius=57.2801 StartAngle=0.0137959 EndAngle=3.15539
    g2: LineSegment StartX=113.108 StartY=143.79 StartZ=0 EndX=57.2747 EndY=143.02 EndZ=0
    g3: LineSegment StartX=-113.108 StartY=140.669 StartZ=0 EndX=-57.2747 EndY=141.439 EndZ=0
    g4: LineSegment StartX=-57.2747 StartY=141.439 StartZ=0 EndX=0 EndY=142.229 EndZ=0
    g5: LineSegment StartX=0 StartY=142.229 StartZ=0 EndX=57.2747 EndY=143.02 EndZ=0
  constraints (13):
    c: Coincident(g1,g0)
    c: Coincident(g2,g0)
    c: Coincident(g2,g1)
    c: Coincident(g3,g0)
    c: Coincident(g3,g1)
    c: Coincident(g4,g1)
    c: Coincident(g4,g0)
    c: Coincident(g5,g0)
    c: Coincident(g5,g1)
    c: Tangent(g2,g5)
    c: Tangent(g4,g3)
    c: Angle(g5,g4) = 3.14159
    c: PointOnObject(g0,g-2)
FEATURE [PartDesign::Pocket] Pocket001
  BaseFeature = -> Pocket
  Direction = (-1,2e-16,-3e-16)
  Length = 5
  Length2 = 5
  Profile = -> Sketch105
  ReferenceAxis = -> Sketch105 [N_Axis]
  Type = 0
FEATURE [PartDesign::Body] Body  label="B_Y_Axis_Base_Left"
  Group = -> [Sketch,Pad,Sketch001,Hole,Sketch002,Pad001,Sketch104,Pocket,Sketch105,Pocket001]
  Origin = -> Origin001
  Tip = -> Pocket001
FEATURE [App::Part] Part  label="P_Y_Axis_Base_Left"
  Group = -> [Body,LCS_Y_Axis_Base_Left_Bolt1,LCS_Y_Axis_Base_Left_Bolt0,LCS_Y_Axis_Base_Left_Bolt2,LCS_Y_Axis_Base_Left_Bolt3,LCS_Y_Axis_Base_Left_Origin,LCS_Y_Axis_Base_Pivot,LCS_Y_Axis_Base_Left_MotorMount]
  Origin = -> Origin
FEATURE [Sketcher::SketchObject] Sketch106
  FullyConstrained = true
  MapMode = 5
  Placement = pos=(0,0,0) rot=(0.57735,0.57735,0.57735;2.0944rad)
  Support = -> [YZ_Plane005]
  sketch-geometry (1):
    g0: Circle CenterX=0 CenterY=0 CenterZ=0 NormalX=0 NormalY=0 NormalZ=1 AngleXU=0 Radius=25
  constraints (2):
    c: Coincident(g0,g-1)
    c: Diameter(g0) = 50
FEATURE [PartDesign::Pad] Pad003
  Direction = (1,-2e-16,3e-16)
  Length = 10
  Length2 = 10
  Placement = pos=(0,0,0) rot=(1,1,1;2.0944rad)
  Profile = -> Sketch106
  ReferenceAxis = -> Sketch106 [N_Axis]
  Type = 0
FEATURE [PartDesign::CoordinateSystem] LCS_Origin
  AttacherType = Attacher::AttachEngine3D
FEATURE [Sketcher::SketchObject] Sketch107
  FullyConstrained = true
  MapMode = 5
  Placement = pos=(0,0,0) rot=(0.57735,0.57735,0.57735;2.0944rad)
  Support = -> [YZ_Plane005]
  sketch-geometry (1):
    g0: Circle CenterX=0 CenterY=0 CenterZ=0 NormalX=0 NormalY=0 NormalZ=1 AngleXU=0 Radius=10
  constraints (2):
    c: Coincident(g0,g-1)
    c: Diameter(g0) = 20
FEATURE [PartDesign::Pad] Pad004
  BaseFeature = -> Pad003
  Direction = (1,-2e-16,3e-16)
  Length = 50
  Length2 = 10
  Placement = pos=(0,0,0) rot=(1,1,1;2.0944rad)
  Profile = -> Sketch107
  ReferenceAxis = -> Sketch107 [N_Axis]
  Type = 0
FEATURE [Sketcher::SketchObject] Sketch108
  AttachmentOffset = pos=(0,0,40) rot=(0,0,1;0rad)
  FullyConstrained = false
  MapMode = 5
  Placement = pos=(40,-8.9e-15,8.9e-15) rot=(0.57735,0.57735,0.57735;2.0944rad)
  Support = -> [YZ_Plane005]
  sketch-geometry (1):
    g0: Circle CenterX=0 CenterY=0 CenterZ=0 NormalX=0 NormalY=0 NormalZ=1 AngleXU=0 Radius=13.9399
  constraints (1):
    c: Coincident(g0,g-1)
FEATURE [PartDesign::Pad] Pad005
  BaseFeature = -> Pad004
  Direction = (1,-2e-16,3e-16)
  Length = 20
  Length2 = 10
  Placement = pos=(0,0,0) rot=(1,1,1;2.0944rad)
  Profile = -> Sketch108
  ReferenceAxis = -> Sketch108 [N_Axis]
  Type = 0
FEATURE [PartDesign::Body] Body002  label="Body"
  Group = -> [Sketch106,Pad003,Sketch107,Pad004,Sketch108,Pad005]
  Origin = -> Origin005
  Tip = -> Pad005
FEATURE [App::Part] Part002  label="P_Y_Axis_RotorWheel"
  Group = -> [Body002,LCS_Origin]
  Origin = -> Origin004
FEATURE [App::DocumentObjectGroup] Group  label="Parts"
  Group = -> [Part,Part001,Part002]
---- part standard-parts.FCStd = doc fcstd_9b47ef122aeb (208734 chars; too large to inline — full recipe in that document) ----
